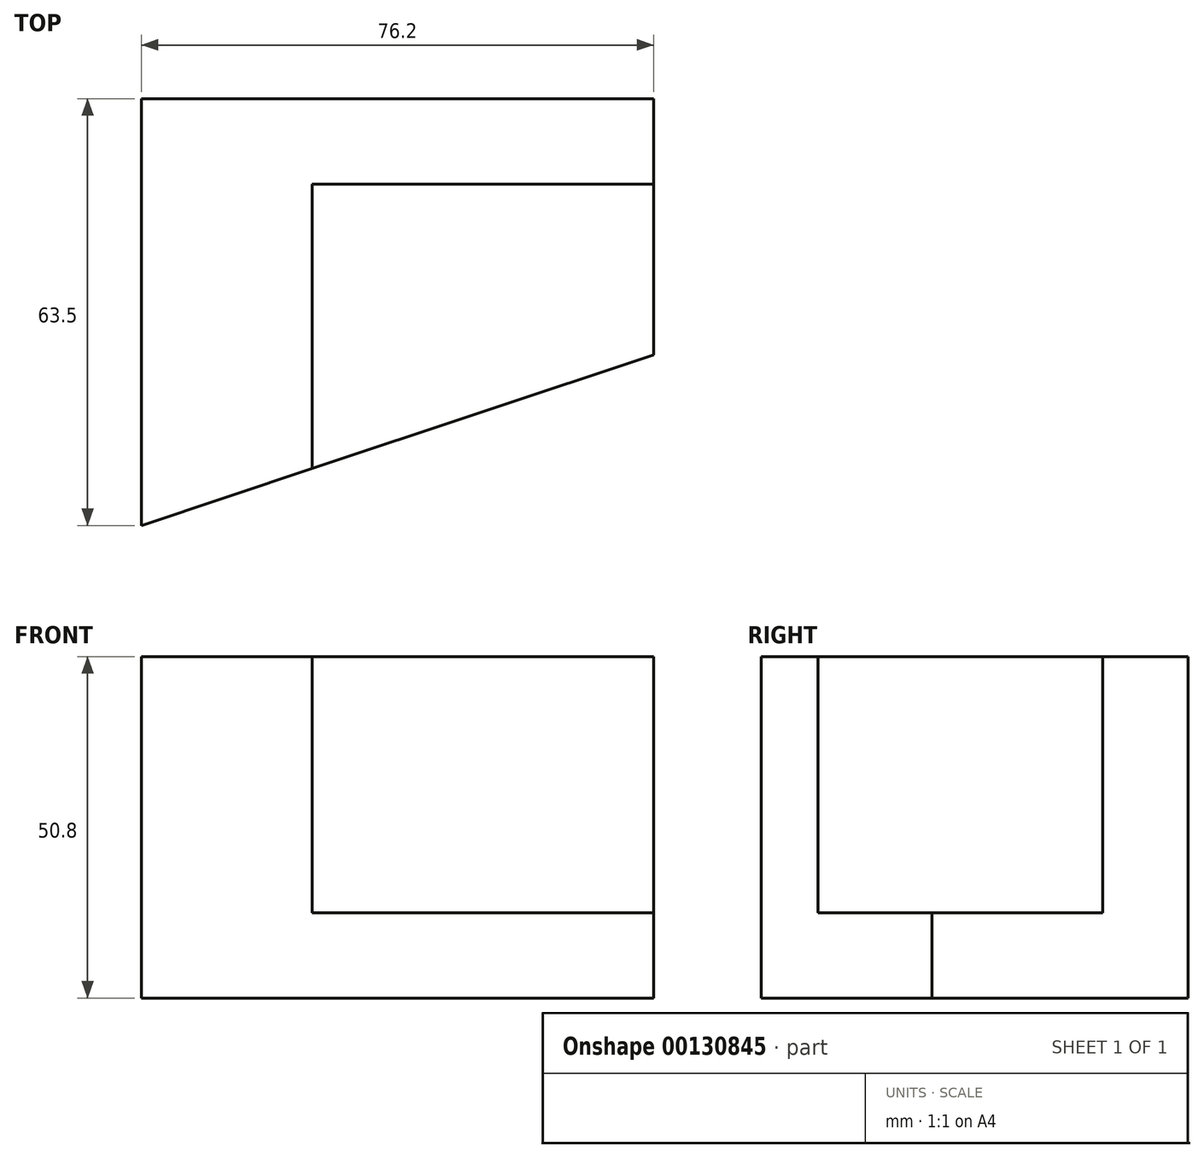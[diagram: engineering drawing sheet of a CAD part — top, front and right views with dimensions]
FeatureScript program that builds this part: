
annotation { "Feature Type Name" : "Feature", "Feature Type Description" : "" }
export const myFeature = defineFeature(function(context is Context, id is Id, definition is map)
    precondition{}
    {
        {
            var Q0;
            Q0=qCreatedBy(makeId("Front.planeOp"),FACE);
            var sketch = newSketch(context, id + "F0", { "sketchPlane" : qUnion([Q0])});
            skLineSegment(sketch, "E0.bottom", {"start": v(0, 0) * mm, "end": v(76.2, 0) * mm});
            skLineSegment(sketch, "E0.top", {"start": v(0, 50.8) * mm, "end": v(76.2, 50.8) * mm});
            skLineSegment(sketch, "E0.left", {"start": v(0, 0) * mm, "end": v(0, 50.8) * mm});
            skLineSegment(sketch, "E0.right", {"start": v(76.2, 0) * mm, "end": v(76.2, 50.8) * mm});
            skSolve(sketch);
        }
        {
            var Q0;
            Q0 = qSketchRegion(id + "F0", true);
            extrude(context, id + "F1", {"entities" : qUnion([Q0]), "depth" : 63.5 * mm});
        }
        {
            var Q0;
            Q0=qCreatedBy(makeId("Top.planeOp"),FACE);
            var sketch = newSketch(context, id + "F2", { "sketchPlane" : qUnion([Q0])});
            skLineSegment(sketch, "E1", {"start": v(0, -63.5) * mm, "end": v(76.2, -38.1) * mm});
            skLineSegment(sketch, "E2", {"start": v(0, -63.5) * mm, "end": v(76.2, -63.5) * mm});
            skLineSegment(sketch, "E3", {"start": v(76.2, -63.5) * mm, "end": v(76.2, -38.1) * mm});
            skSolve(sketch);
        }
        {
            var Q0;
            Q0 = qSketchRegion(id + "F2", true);
            extrude(context, id + "F3", {"entities" : qUnion([Q0]), "operationType" : NewBodyOperationType.REMOVE, "endBound" : BoundingType.THROUGH_ALL, "depth" : 50.8 * mm});
        }
        {
            var Q0;
            Q0=qCreatedBy(makeId("Front.planeOp"),FACE);
            var sketch = newSketch(context, id + "F4", { "sketchPlane" : qUnion([Q0])});
            skLineSegment(sketch, "E4.bottom", {"start": v(76.2, 12.7) * mm, "end": v(25.4, 12.7) * mm});
            skLineSegment(sketch, "E4.top", {"start": v(76.2, 50.8) * mm, "end": v(25.4, 50.8) * mm});
            skLineSegment(sketch, "E4.left", {"start": v(76.2, 12.7) * mm, "end": v(76.2, 50.8) * mm});
            skLineSegment(sketch, "E4.right", {"start": v(25.4, 12.7) * mm, "end": v(25.4, 50.8) * mm});
            skSolve(sketch);
        }
        {
            var Q0;
            Q0 = qSketchRegion(id + "F4", true);
            extrude(context, id + "F5", {"entities" : qUnion([Q0]), "operationType" : NewBodyOperationType.REMOVE, "depth" : 63.5 * mm});
        }
        {
            var Q0;
            Q0 = qSketchRegion(id + "F4", true);
            extrude(context, id + "F6", {"entities" : qUnion([Q0]), "operationType" : NewBodyOperationType.ADD, "depth" : 12.7 * mm});
        }
    });
